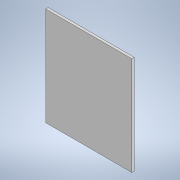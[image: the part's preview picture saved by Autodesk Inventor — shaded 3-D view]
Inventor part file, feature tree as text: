
AUTODESK INVENTOR PART (.ipt)
format: ipt  version: 2021 (Build 250183000, 183)  size: 90,624 bytes
history: native  units: mm
features: extrude x1, sketch x1
ambient origin geometry x8: Origin, YZ Plane, XZ Plane, XY Plane, X Axis, Y Axis, Z Axis, Center Point
bodies: Solid1 (feature_tree)
feature tree (2):
  extrude  "Extrusion1"  Depth=81.0mm
  sketch  "Sketch1"  dims[d0=70.8mm d1=81.0mm d2=2.0mm d3=0.0mm d8=0.5mm d9=0.872665mm d10=0.5mm d11=0.872665mm]
